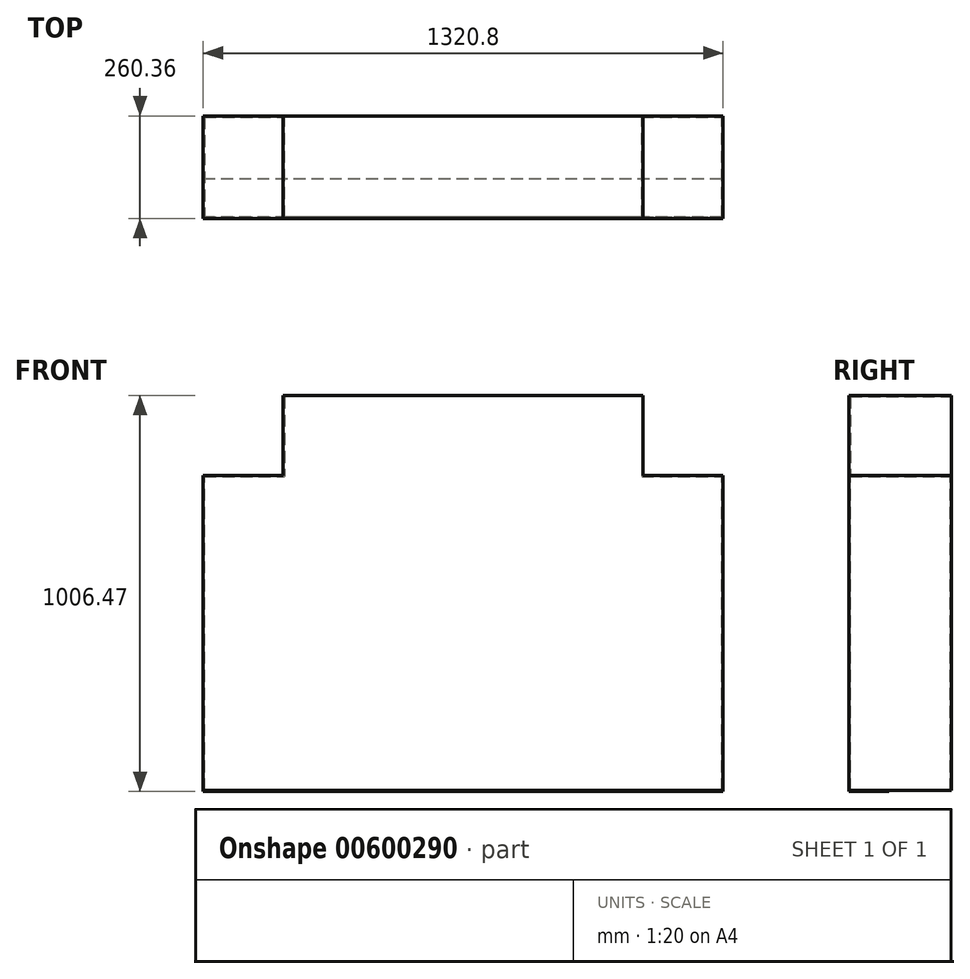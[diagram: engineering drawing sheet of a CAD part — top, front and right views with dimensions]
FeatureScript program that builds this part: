
annotation { "Feature Type Name" : "Feature", "Feature Type Description" : "" }
export const myFeature = defineFeature(function(context is Context, id is Id, definition is map)
    precondition{}
    {
        {
            var Q0;
            Q0=qCreatedBy(makeId("Right.planeOp"),FACE);
            var sketch = newSketch(context, id + "F0", { "sketchPlane" : qUnion([Q0])});
            skLineSegment(sketch, "E0.bottom", {"start": v(127, 0) * mm, "end": v(-127, 0) * mm});
            skLineSegment(sketch, "E0.top", {"start": v(127, 1000.13) * mm, "end": v(-127, 1000.13) * mm});
            skLineSegment(sketch, "E0.left", {"start": v(127, 0) * mm, "end": v(127, 1000.13) * mm});
            skLineSegment(sketch, "E0.right", {"start": v(-127, 0) * mm, "end": v(-127, 1000.13) * mm});
            skLineSegment(sketch, "E1.bottom", {"start": v(130.18, 0) * mm, "end": v(-130.18, 0) * mm});
            skLineSegment(sketch, "E1.top", {"start": v(130.18, 1003.3) * mm, "end": v(-130.18, 1003.3) * mm});
            skLineSegment(sketch, "E1.left", {"start": v(130.18, 0) * mm, "end": v(130.18, 1003.3) * mm});
            skLineSegment(sketch, "E1.right", {"start": v(-130.18, 0) * mm, "end": v(-130.18, 1003.3) * mm});
            skLineSegment(sketch, "E2", {"start": v(0, 0) * mm, "end": v(0, 13.55) * mm, "construction": true});
            skSolve(sketch);
        }
        {
            var Q0;
            Q0=makeQuery(id+"F0.imprint","IMPRINT",FACE,{"disambiguationData":[TD([[makeQuery(id+"F0.imprint","IMPRINT",EDGE,{"derivedFrom":sQuery(id+"F0.wireOp",EDGE,"E0.top")}),-1.0]])]});
            extrude(context, id + "F1", {"entities" : qUnion([Q0]), "depth" : 1314.45 * mm, "offsetDistance" : 25.4 * mm, "symmetric" : true});
        }
        {
            var Q0;
            Q0=makeQuery(id+"F1.opExtrude","CAP_FACE",FACE,{"disambiguationData":[OSD([sQuery(id+"F0.wireOp",EDGE,"E0.top"),sQuery(id+"F0.wireOp",EDGE,"E0.left"),sQuery(id+"F0.wireOp",EDGE,"E0.right"),sQuery(id+"F0.wireOp",EDGE,"E1.bottom"),sQuery(id+"F0.wireOp",EDGE,"E1.top"),sQuery(id+"F0.wireOp",EDGE,"E1.left"),sQuery(id+"F0.wireOp",EDGE,"E1.right")])],"isStart":true});
            var sketch = newSketch(context, id + "F2", { "sketchPlane" : qUnion([Q0])});
            skLineSegment(sketch, "E3.0", {"start": v(-130.18, 1003.3) * mm, "end": v(130.18, 1003.3) * mm});
            skLineSegment(sketch, "E3.1", {"start": v(-130.18, 0) * mm, "end": v(-130.18, 1003.3) * mm});
            skLineSegment(sketch, "E3.2", {"start": v(130.18, 0) * mm, "end": v(130.18, 1003.3) * mm});
            skLineSegment(sketch, "E4", {"start": v(-127, 0) * mm, "end": v(127, 0) * mm});
            skSolve(sketch);
        }
        {
            var Q0;
            Q0 = qSketchRegion(id + "F2", true);
            var Q1;
            Q1=makeQuery(id+"F2.imprint","IMPRINT",FACE,{"disambiguationData":[TD([[makeQuery(id+"F2.imprint","IMPRINT",EDGE,{"derivedFrom":sQuery(id+"F2.wireOp",EDGE,"E4")}),1.0]])]});
            var Q2;
            Q2=makeQuery(id+"F2.imprint","IMPRINT",FACE,{"disambiguationData":[TD([[makeQuery(id+"F2.imprint","IMPRINT",EDGE,{"derivedFrom":sQuery(id+"F2.wireOp",EDGE,"E3.0")}),-1.0]])]});
            extrude(context, id + "F3", {"entities" : qUnion([Q0, Q1, Q2]), "operationType" : NewBodyOperationType.ADD, "depth" : 3.17 * mm, "offsetDistance" : 25.4 * mm});
        }
        {
            var Q0;
            Q0=makeQuery(id+"F1.opExtrude","CAP_FACE",FACE,{"disambiguationData":[OSD([sQuery(id+"F0.wireOp",EDGE,"E0.top"),sQuery(id+"F0.wireOp",EDGE,"E0.left"),sQuery(id+"F0.wireOp",EDGE,"E0.right"),sQuery(id+"F0.wireOp",EDGE,"E1.bottom"),sQuery(id+"F0.wireOp",EDGE,"E1.top"),sQuery(id+"F0.wireOp",EDGE,"E1.left"),sQuery(id+"F0.wireOp",EDGE,"E1.right")])],"isStart":false});
            var sketch = newSketch(context, id + "F4", { "sketchPlane" : qUnion([Q0])});
            skLineSegment(sketch, "E5.0", {"start": v(-130.18, 1003.3) * mm, "end": v(130.18, 1003.3) * mm});
            skLineSegment(sketch, "E5.1", {"start": v(-130.18, 0) * mm, "end": v(-130.18, 1003.3) * mm});
            skLineSegment(sketch, "E5.2", {"start": v(130.18, 0) * mm, "end": v(130.17, 1003.3) * mm});
            skLineSegment(sketch, "E6", {"start": v(-130.18, 0) * mm, "end": v(130.18, 0) * mm});
            skSolve(sketch);
        }
        {
            var Q0;
            Q0 = qSketchRegion(id + "F4", true);
            extrude(context, id + "F5", {"entities" : qUnion([Q0]), "operationType" : NewBodyOperationType.ADD, "depth" : 3.17 * mm, "offsetDistance" : 25.4 * mm});
        }
        {
            var Q0;
            {var subQ0=sQuery(id+"F0.wireOp",EDGE,"E1.bottom");Q0=makeQuery(id+"F5.boolean.opBoolean","MERGE",FACE,{"derivedFrom":[makeQuery(id+"F3.boolean.opBoolean","MERGE",FACE,{"derivedFrom":[makeQuery(id+"F1.opExtrude","SWEPT_FACE",FACE,{"disambiguationData":[OSD([subQ0]),TDD([makeQuery(id+"F0.imprint","IMPRINT",EDGE,{"disambiguationData":[TD([[makeQuery(id+"F0.imprint","INTERSECT",VERTEX,{"derivedFrom":[sQuery(id+"F0.wireOp",EDGE,"E0.left"),subQ0]}),1.0]])],"derivedFrom":subQ0})])]}),makeQuery(id+"F1.opExtrude","SWEPT_FACE",FACE,{"disambiguationData":[OSD([subQ0]),TDD([makeQuery(id+"F0.imprint","IMPRINT",EDGE,{"disambiguationData":[TD([[makeQuery(id+"F0.imprint","INTERSECT",VERTEX,{"derivedFrom":[sQuery(id+"F0.wireOp",EDGE,"E0.right"),subQ0]}),-1.0]])],"derivedFrom":subQ0})])]}),makeQuery(id+"F3.opExtrude","SWEPT_FACE",FACE,{"disambiguationData":[OSD([subQ0,sQuery(id+"F2.wireOp",EDGE,"E4")])]})]}),makeQuery(id+"F5.opExtrude","SWEPT_FACE",FACE,{"disambiguationData":[OSD([sQuery(id+"F4.wireOp",EDGE,"E6")])]})]});}
            var sketch = newSketch(context, id + "F6", { "sketchPlane" : qUnion([Q0])});
            skLineSegment(sketch, "E7.bottom", {"start": v(-660.4, 130.18) * mm, "end": v(660.4, 130.18) * mm});
            skLineSegment(sketch, "E7.top", {"start": v(-660.4, 28.58) * mm, "end": v(660.4, 28.58) * mm});
            skLineSegment(sketch, "E7.left", {"start": v(-660.4, 130.18) * mm, "end": v(-660.4, 28.58) * mm});
            skLineSegment(sketch, "E7.right", {"start": v(660.4, 130.18) * mm, "end": v(660.4, 28.58) * mm});
            skSolve(sketch);
        }
        {
            var Q0;
            Q0 = qSketchRegion(id + "F6", true);
            extrude(context, id + "F7", {"entities" : qUnion([Q0]), "depth" : 3.17 * mm, "offsetDistance" : 25.4 * mm});
        }
        {
            var Q0;
            Q0=makeQuery(id+"F5.boolean.opBoolean","MERGE",FACE,{"derivedFrom":[makeQuery(id+"F3.boolean.opBoolean","MERGE",FACE,{"derivedFrom":[makeQuery(id+"F1.opExtrude","SWEPT_FACE",FACE,{"disambiguationData":[OSD([sQuery(id+"F0.wireOp",EDGE,"E1.right")])]}),makeQuery(id+"F3.opExtrude","SWEPT_FACE",FACE,{"disambiguationData":[OSD([sQuery(id+"F2.wireOp",EDGE,"E3.2")])]})]}),makeQuery(id+"F5.opExtrude","SWEPT_FACE",FACE,{"disambiguationData":[OSD([sQuery(id+"F4.wireOp",EDGE,"E5.1")])]})]});
            var sketch = newSketch(context, id + "F8", { "sketchPlane" : qUnion([Q0])});
            skLineSegment(sketch, "E8.bottom", {"start": v(-734.49, 1046.23) * mm, "end": v(-457.2, 1046.23) * mm});
            skLineSegment(sketch, "E8.top", {"start": v(-734.49, 800.1) * mm, "end": v(-457.2, 800.1) * mm});
            skLineSegment(sketch, "E8.left", {"start": v(-734.49, 1046.23) * mm, "end": v(-734.49, 800.1) * mm});
            skLineSegment(sketch, "E8.right", {"start": v(-457.2, 1046.23) * mm, "end": v(-457.2, 800.1) * mm});
            skLineSegment(sketch, "E9.bottom", {"start": v(847.01, 1046.23) * mm, "end": v(457.2, 1046.23) * mm});
            skLineSegment(sketch, "E9.top", {"start": v(847.01, 800.1) * mm, "end": v(457.2, 800.1) * mm});
            skLineSegment(sketch, "E9.left", {"start": v(847.01, 1046.23) * mm, "end": v(847.01, 800.1) * mm});
            skLineSegment(sketch, "E9.right", {"start": v(457.2, 1046.23) * mm, "end": v(457.2, 800.1) * mm});
            skSolve(sketch);
        }
        {
            var Q0;
            Q0 = qSketchRegion(id + "F8", true);
            extrude(context, id + "F9", {"entities" : qUnion([Q0]), "operationType" : NewBodyOperationType.REMOVE, "endBound" : BoundingType.THROUGH_ALL, "oppositeDirection" : true, "depth" : 25.4 * mm, "offsetDistance" : 25.4 * mm});
        }
        {
            var Q0;
            Q0=makeQuery(id+"F5.boolean.opBoolean","MERGE",FACE,{"derivedFrom":[makeQuery(id+"F3.boolean.opBoolean","MERGE",FACE,{"derivedFrom":[makeQuery(id+"F1.opExtrude","SWEPT_FACE",FACE,{"disambiguationData":[OSD([sQuery(id+"F0.wireOp",EDGE,"E1.right")])]}),makeQuery(id+"F3.opExtrude","SWEPT_FACE",FACE,{"disambiguationData":[OSD([sQuery(id+"F2.wireOp",EDGE,"E3.2")])]})]}),makeQuery(id+"F5.opExtrude","SWEPT_FACE",FACE,{"disambiguationData":[OSD([sQuery(id+"F4.wireOp",EDGE,"E5.1")])]})]});
            var sketch = newSketch(context, id + "F10", { "sketchPlane" : qUnion([Q0])});
            skLineSegment(sketch, "E10.0", {"start": v(-660.4, 800.1) * mm, "end": v(-457.2, 800.1) * mm});
            skLineSegment(sketch, "E10.1", {"start": v(-457.2, 1003.3) * mm, "end": v(-457.2, 800.1) * mm});
            skLineSegment(sketch, "E10.2", {"start": v(457.2, 1003.3) * mm, "end": v(457.2, 800.1) * mm});
            skLineSegment(sketch, "E10.3", {"start": v(657.23, 800.1) * mm, "end": v(457.2, 800.1) * mm});
            skLineSegment(sketch, "E11.bottom", {"start": v(457.2, 1003.3) * mm, "end": v(454.03, 1003.3) * mm});
            skLineSegment(sketch, "E11.top", {"start": v(457.2, 796.93) * mm, "end": v(454.03, 796.93) * mm});
            skLineSegment(sketch, "E11.left", {"start": v(457.2, 1003.3) * mm, "end": v(457.2, 796.92) * mm});
            skLineSegment(sketch, "E11.right", {"start": v(454.03, 1003.3) * mm, "end": v(454.03, 796.93) * mm});
            skLineSegment(sketch, "E12.bottom", {"start": v(454.03, 796.93) * mm, "end": v(660.4, 796.93) * mm});
            skLineSegment(sketch, "E12.top", {"start": v(454.03, 800.1) * mm, "end": v(660.4, 800.1) * mm});
            skLineSegment(sketch, "E12.left", {"start": v(454.03, 796.93) * mm, "end": v(454.03, 800.1) * mm});
            skLineSegment(sketch, "E12.right", {"start": v(660.4, 796.93) * mm, "end": v(660.4, 800.1) * mm});
            skLineSegment(sketch, "E13.bottom", {"start": v(-660.4, 800.1) * mm, "end": v(-454.03, 800.1) * mm});
            skLineSegment(sketch, "E13.top", {"start": v(-660.4, 796.92) * mm, "end": v(-454.03, 796.92) * mm});
            skLineSegment(sketch, "E13.left", {"start": v(-660.4, 800.1) * mm, "end": v(-660.4, 796.92) * mm});
            skLineSegment(sketch, "E13.right", {"start": v(-454.03, 800.1) * mm, "end": v(-454.03, 796.92) * mm});
            skLineSegment(sketch, "E14.bottom", {"start": v(-454.03, 800.1) * mm, "end": v(-457.2, 800.1) * mm});
            skLineSegment(sketch, "E14.top", {"start": v(-454.03, 1003.3) * mm, "end": v(-457.2, 1003.3) * mm});
            skLineSegment(sketch, "E14.left", {"start": v(-454.03, 800.1) * mm, "end": v(-454.03, 1003.3) * mm});
            skLineSegment(sketch, "E14.right", {"start": v(-457.2, 800.1) * mm, "end": v(-457.2, 1003.3) * mm});
            skSolve(sketch);
        }
        {
            var Q0;
            Q0 = qSketchRegion(id + "F10", true);
            var Q1;
            Q1=makeQuery(id+"F5.boolean.opBoolean","MERGE",FACE,{"derivedFrom":[makeQuery(id+"F3.boolean.opBoolean","MERGE",FACE,{"derivedFrom":[makeQuery(id+"F1.opExtrude","SWEPT_FACE",FACE,{"disambiguationData":[OSD([sQuery(id+"F0.wireOp",EDGE,"E1.left")])]}),makeQuery(id+"F3.opExtrude","SWEPT_FACE",FACE,{"disambiguationData":[OSD([sQuery(id+"F2.wireOp",EDGE,"E3.1")])]})]}),makeQuery(id+"F5.opExtrude","SWEPT_FACE",FACE,{"disambiguationData":[OSD([sQuery(id+"F4.wireOp",EDGE,"E5.2")])]})]});
            extrude(context, id + "F11", {"entities" : qUnion([Q0]), "operationType" : NewBodyOperationType.ADD, "endBound" : BoundingType.UP_TO_SURFACE, "oppositeDirection" : true, "depth" : 25.4 * mm, "endBoundEntityFace" : qUnion([Q1]), "offsetDistance" : 25.4 * mm});
        }
    });
